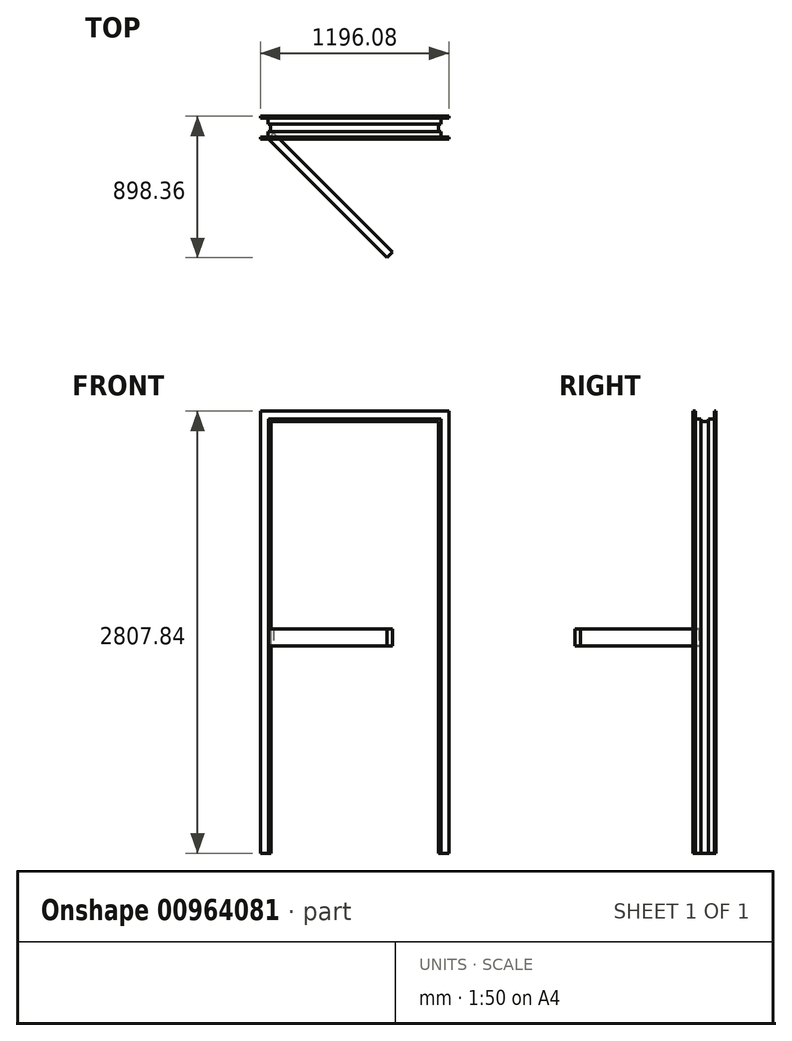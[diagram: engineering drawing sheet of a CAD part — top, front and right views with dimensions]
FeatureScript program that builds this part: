
annotation { "Feature Type Name" : "Feature", "Feature Type Description" : "" }
export const myFeature = defineFeature(function(context is Context, id is Id, definition is map)
    precondition{}
    {
        {
            assignVariable(context, id + "F0", {"name" : "Length", "anyValue" : 108});
        }
        {
            var Q0;
            Q0=qCreatedBy(makeId("Front.planeOp"),FACE);
            var sketch = newSketch(context, id + "F1", { "sketchPlane" : qUnion([Q0])});
            skLineSegment(sketch, "E0.bottom", {"start": v(533.4, -1371.6) * mm, "end": v(-533.4, -1371.6) * mm});
            skLineSegment(sketch, "E0.top", {"start": v(533.4, 1371.6) * mm, "end": v(-533.4, 1371.6) * mm});
            skLineSegment(sketch, "E0.left", {"start": v(533.4, -1371.6) * mm, "end": v(533.4, 1371.6) * mm});
            skLineSegment(sketch, "E0.right", {"start": v(-533.4, -1371.6) * mm, "end": v(-533.4, 1371.6) * mm});
            skPoint(sketch, "E0.middle", {"position": v(0, 0) * mm});
            skSolve(sketch);
        }
        {
            var Q0;
            Q0=qCreatedBy(makeId("Top.planeOp"),FACE);
            var sketch = newSketch(context, id + "F2", { "sketchPlane" : qUnion([Q0])});
            skLineSegment(sketch, "E1", {"start": v(-533.4, 23.37) * mm, "end": v(-533.4, -23.37) * mm});
            skLineSegment(sketch, "E2", {"start": v(-533.4, -23.37) * mm, "end": v(-549.27, -23.37) * mm});
            skLineSegment(sketch, "E3", {"start": v(-549.27, -23.37) * mm, "end": v(-549.27, -71) * mm});
            skLineSegment(sketch, "E4", {"start": v(-549.27, -71) * mm, "end": v(-596.01, -71) * mm});
            skLineSegment(sketch, "E5", {"start": v(-596.01, -71) * mm, "end": v(-596.01, -60.32) * mm});
            skLineSegment(sketch, "E6", {"start": v(-489.55, 0) * mm, "end": v(-533.4, 0) * mm, "construction": true});
            skLineSegment(sketch, "E7.MirrorCS", {"start": v(-533.4, 23.37) * mm, "end": v(-549.27, 23.37) * mm});
            skLineSegment(sketch, "E8.MirrorCS", {"start": v(-549.27, 23.37) * mm, "end": v(-549.27, 71) * mm});
            skLineSegment(sketch, "E9.MirrorCS", {"start": v(-549.27, 71) * mm, "end": v(-596.01, 71) * mm});
            skLineSegment(sketch, "E10.MirrorCS", {"start": v(-596.01, 71) * mm, "end": v(-596.01, 60.32) * mm});
            skLineSegment(sketch, "E11.MirrorCS", {"start": v(-533.4, -23.37) * mm, "end": v(-533.4, 23.37) * mm});
            skLineSegment(sketch, "E12.0", {"start": v(-598.04, 73.03) * mm, "end": v(-598.04, 60.32) * mm});
            skLineSegment(sketch, "E12.1", {"start": v(-547.24, 73.03) * mm, "end": v(-598.04, 73.03) * mm});
            skLineSegment(sketch, "E12.2", {"start": v(-547.24, 25.4) * mm, "end": v(-547.24, 73.03) * mm});
            skLineSegment(sketch, "E12.3", {"start": v(-531.37, 25.4) * mm, "end": v(-547.24, 25.4) * mm});
            skLineSegment(sketch, "E12.4", {"start": v(-531.37, -25.4) * mm, "end": v(-531.37, 25.4) * mm});
            skLineSegment(sketch, "E12.5", {"start": v(-598.04, -73.02) * mm, "end": v(-598.04, -60.32) * mm});
            skLineSegment(sketch, "E12.6", {"start": v(-547.24, -73.02) * mm, "end": v(-598.04, -73.02) * mm});
            skLineSegment(sketch, "E12.7", {"start": v(-547.24, -25.4) * mm, "end": v(-547.24, -73.02) * mm});
            skLineSegment(sketch, "E12.8", {"start": v(-531.37, -25.4) * mm, "end": v(-547.24, -25.4) * mm});
            skLineSegment(sketch, "E13", {"start": v(-598.04, 60.32) * mm, "end": v(-596.01, 60.32) * mm});
            skLineSegment(sketch, "E14", {"start": v(-598.04, -60.32) * mm, "end": v(-596.01, -60.32) * mm});
            skSolve(sketch);
        }
        {
            var Q0;
            Q0=qSketchRegion(id+"F2",true);
            var Q1;
            Q1=sQuery(id+"F1.wireOp",EDGE,"E0.right");
            var Q2;
            Q2=sQuery(id+"F1.wireOp",EDGE,"E0.top");
            var Q3;
            Q3=sQuery(id+"F1.wireOp",EDGE,"E0.left");
            sweep(context, id + "F3", {"profiles" : qUnion([Q0]), "path" : qUnion([Q1, Q2, Q3])});
        }
        {
            var Q0;
            Q0=qCreatedBy(makeId("Top.planeOp"),FACE);
            var sketch = newSketch(context, id + "F4", { "sketchPlane" : qUnion([Q0])});
            skLineSegment(sketch, "E15", {"start": v(-514.16, -35.07) * mm, "end": v(240.18, -789.41) * mm});
            skLineSegment(sketch, "E16", {"start": v(240.18, -789.41) * mm, "end": v(204.26, -825.33) * mm});
            skLineSegment(sketch, "E17", {"start": v(204.26, -825.33) * mm, "end": v(-550.08, -71) * mm});
            skLineSegment(sketch, "E18", {"start": v(-550.08, -71) * mm, "end": v(-514.16, -35.07) * mm});
            skSolve(sketch);
        }
        {
            var Q0;
            Q0=makeQuery(id+"F4.imprint","IMPRINT",FACE,{"disambiguationData":[TD([[makeQuery(id+"F4.imprint","IMPRINT",EDGE,{"derivedFrom":sQuery(id+"F4.wireOp",EDGE,"E15")}),-1.0]])]});
            extrude(context, id + "F5", {"entities" : qUnion([Q0]), "operationType" : NewBodyOperationType.ADD, "endBound" : BoundingType.SYMMETRIC, "depth" : (getVariable(context, 'Length') - .125) * mm, "offsetDistance" : 25.4 * mm});
        }
    });
